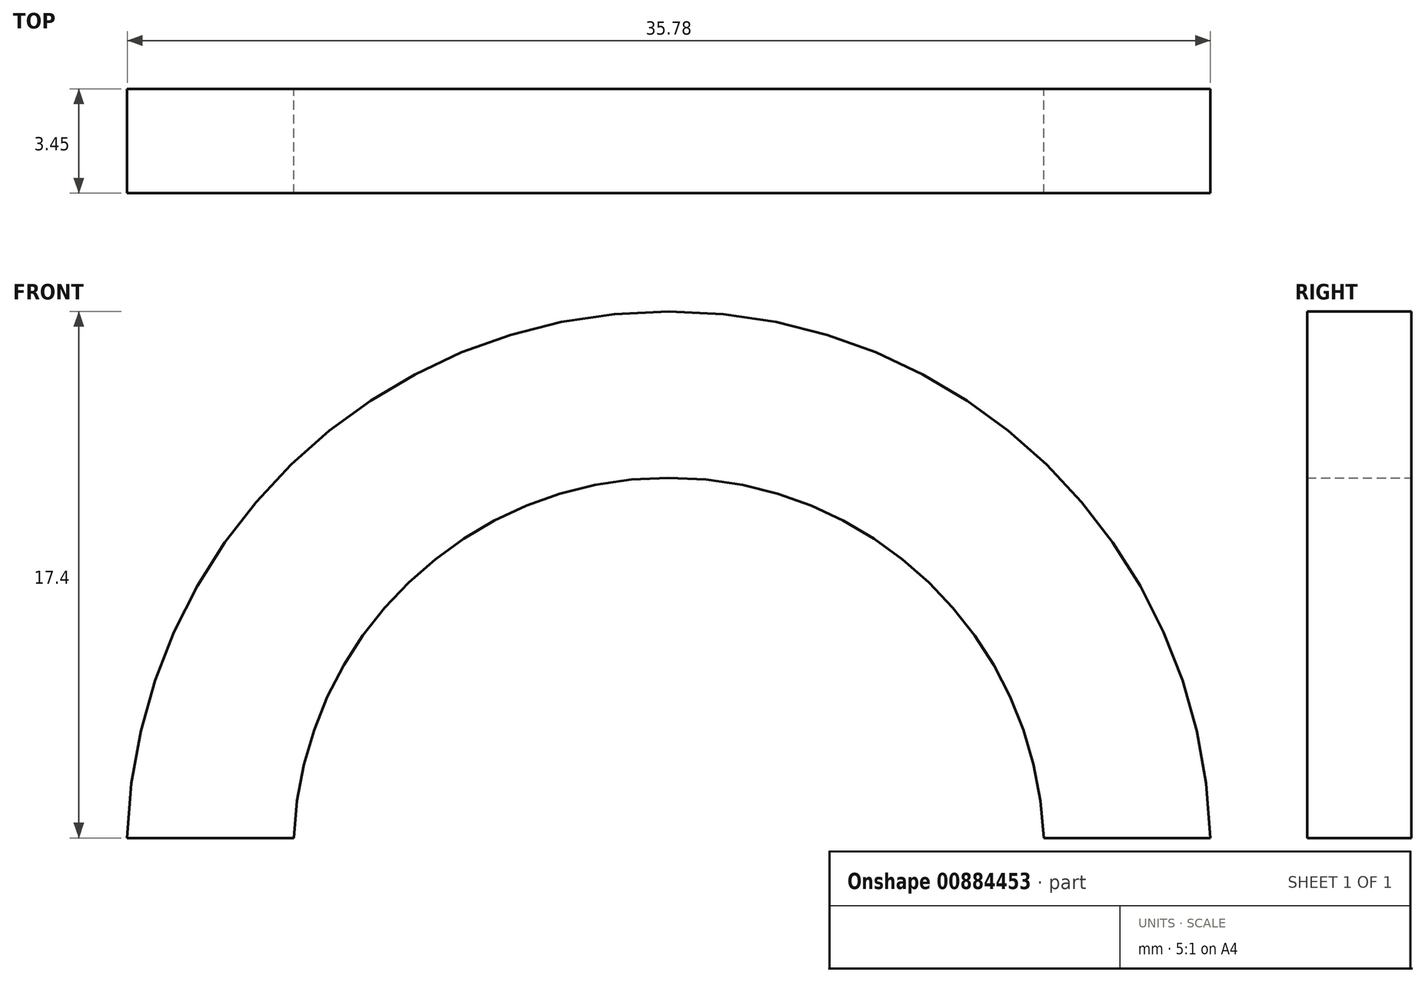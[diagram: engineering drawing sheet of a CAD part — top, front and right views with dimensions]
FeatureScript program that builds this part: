
annotation { "Feature Type Name" : "Feature", "Feature Type Description" : "" }
export const myFeature = defineFeature(function(context is Context, id is Id, definition is map)
    precondition{}
    {
        {
            var Q0;
            Q0=qCreatedBy(makeId("Front.planeOp"),FACE);
            var sketch = newSketch(context, id + "F0", { "sketchPlane" : qUnion([Q0])});
            skLineSegment(sketch, "E0", {"start": v(-50.26, 0.5) * mm, "end": v(46.85, 0.5) * mm, "construction": true});
            skArc(sketch, "E1", {"start": v(-12.39, 0.5) * mm, "mid": v(0, 12.4) * mm, "end": v(12.39, 0.5) * mm});
            skArc(sketch, "E2.0", {"start": v(-17.9, 0.5) * mm, "mid": v(0, 17.9) * mm, "end": v(17.9, 0.5) * mm});
            skLineSegment(sketch, "E3", {"start": v(-12.39, 0.5) * mm, "end": v(-17.9, 0.5) * mm});
            skLineSegment(sketch, "E4", {"start": v(12.39, 0.5) * mm, "end": v(17.9, 0.5) * mm});
            skSolve(sketch);
        }
        {
            var Q0;
            Q0 = qSketchRegion(id + "F0", true);
            extrude(context, id + "F1", {"entities" : qUnion([Q0]), "depth" : 3.45 * mm, "offsetDistance" : 25 * mm});
        }
    });
